# Revit family: CM0016781_Cocina Savona derecha
name_source: partatom
category: Generic Models
units: mm (PartAtom-declared; Revit-internal decimal feet)

## family parameters
Always vertical = Yes
Can host rebar = No
Cut with Voids When Loaded = No
Host = Wall
OmniClass Number = 23.21.23.23.13
OmniClass Title = Residential Food Cookers
Part Type = Normal
Room Calculation Point = No
Round Connector Dimension = Use Diameter
Shared = No

## types (1)
- Ref. CM0016781 COCINA SAVONA 1.80 DERECHA.
    Ancho = 1797 mm
    Carga máxima Mueble Superior = 42 kg.
    Carga máxima mueble inferior = 90 kg.
    Description = Esta cocina de diseño contemporáneo está disponible en una combinación de color Taupé, en su mueble superior, y Coñac en su mueble inferior, generando un contraste de tonos acorde a las tendencias actuales de diseño. Asímismo, se complementa con el detalle de un nicho metálico en el mueble superior.
Sus puertas lisas (sin manijas expuestas) aportan limpieza y continuidad al diseño, lo cual se complementa con un mesón en CoronaStone®. Incluye lavaplatos y cubierta con 4 fogones integrados, además de accesorios como vajillero en acero inoxidable, cajón doble con cubertero y cajón condimentero de dos niveles, para hacer más cómodo tu almacenamiento.
En todo el mueble, los cantos o recubrimiento de bordes cuentan con mayor espesor y rigidez al estándar del mercado, brindando un acabado estético superior y mayor protección a posibles filtraciones de humedad.
Mesón CoronaStone® con lavaplatos y cubierta integrados.
Disfruta de la máxima capacidad de almacenamiento y comodidad en el uso, esta es la solución integral de fácil instalación.
    Dimensiones generales del mueble inferior (H*W*L) = 890 x 592 x 1799mm.
    Dimensiones generales mueble superior (H*W*L). = 613 x 335 x 1799mm.
    Garantía de la madera = 1 año
    Garantía de los herrajes = 1 año
    Garantía del mesón = 10 años
    Height = 875.5 mm
    Manufacturer = Corona
    Material Modulo inferior = Corona_MDP_Taupe
    Material mesón = Corona_Cuarzo
    Material modulo superior = Corona_MDP_Taupe
    Material puertas Modulo inferior = Corona_Madera_Coñac
    Peso Neto aproximado mueble inferior = 67,2 kg.
    Peso Neto aproximado mueble superior = 52,4 kg.
    Profundidad = 577 mm  [stored 1.89304 ft]
    Resistencia a la humedad = Hinchamiento < o =8%.
    URL = https://corona.co

note: [stored X ft] marks values corroborated as IEEE doubles in the binary element streams (Revit-internal decimal feet)

## geometry (parser evidence)
native form markers: Sweep x11
no freeform markers — native parametric forms only
